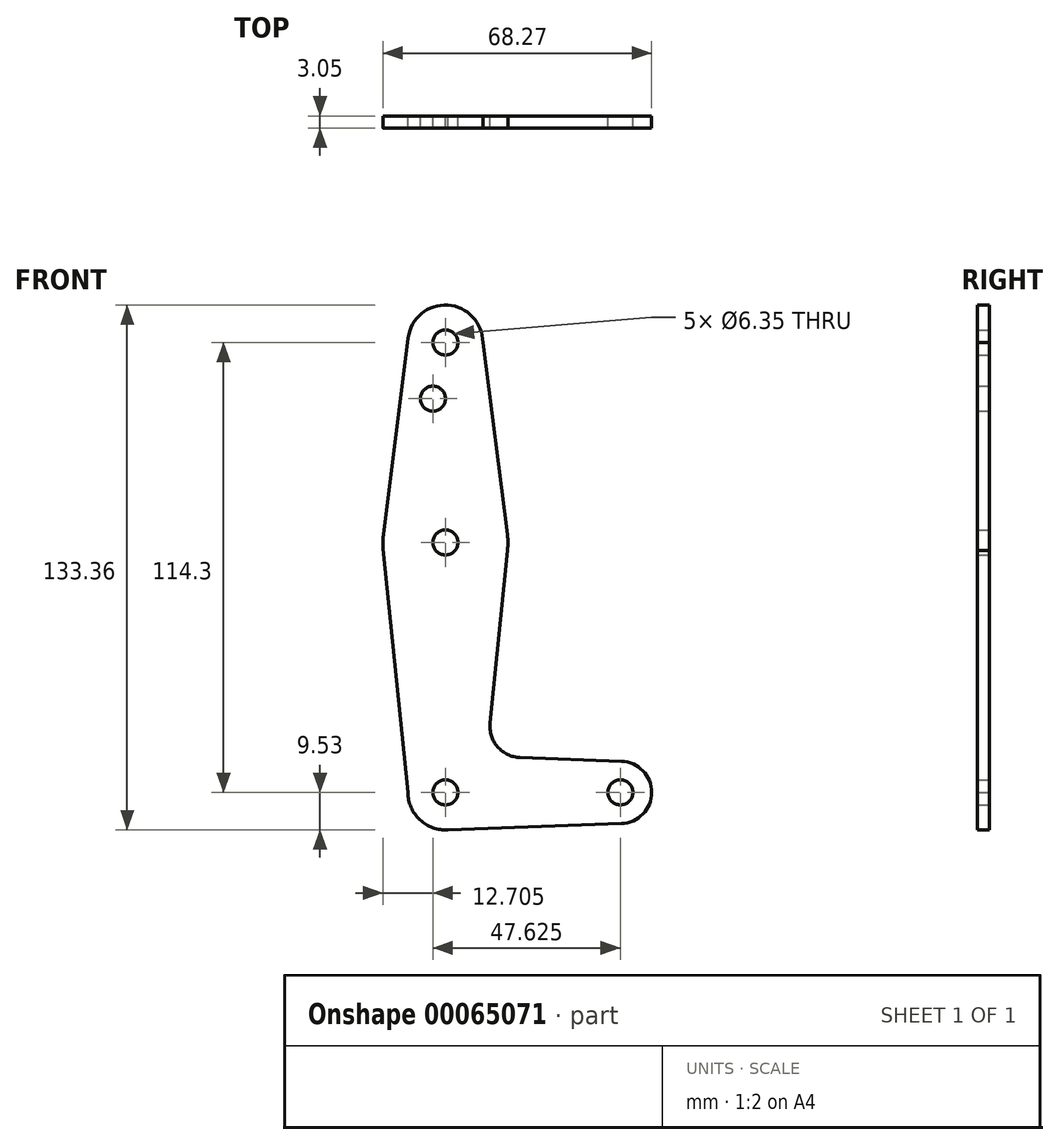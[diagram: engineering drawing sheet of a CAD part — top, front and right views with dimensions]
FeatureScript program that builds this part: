
annotation { "Feature Type Name" : "Feature", "Feature Type Description" : "" }
export const myFeature = defineFeature(function(context is Context, id is Id, definition is map)
    precondition{}
    {
        {
            var Q0;
            Q0=qCreatedBy(makeId("Front.planeOp"),FACE);
            var sketch = newSketch(context, id + "F0", { "sketchPlane" : qUnion([Q0])});
            skLineSegment(sketch, "E0", {"start": v(0, 114.3) * mm, "end": v(0, 0) * mm, "construction": true});
            skLineSegment(sketch, "E1", {"start": v(0, 0) * mm, "end": v(44.45, 0) * mm, "construction": true});
            skCircle(sketch, "E2", {"center": v(0, 114.3) * mm, "radius": 9.53 * mm});
            skCircle(sketch, "E3", {"center": v(0, 63.5) * mm, "radius": 15.88 * mm});
            skCircle(sketch, "E4", {"center": v(0, 0) * mm, "radius": 9.53 * mm});
            skCircle(sketch, "E5", {"center": v(44.45, 0) * mm, "radius": 7.94 * mm});
            skLineSegment(sketch, "E6", {"start": v(44.73, 7.93) * mm, "end": v(18.97, 8.85) * mm});
            skLineSegment(sketch, "E7", {"start": v(0, -9.52) * mm, "end": v(44.73, -7.93) * mm});
            skLineSegment(sketch, "E8", {"start": v(9.53, 114.3) * mm, "end": v(15.75, 65.5) * mm});
            skLineSegment(sketch, "E9", {"start": v(15.75, 61.5) * mm, "end": v(11.34, 17.6) * mm});
            skLineSegment(sketch, "E10", {"start": v(-9.53, 0) * mm, "end": v(-15.8, 61.9) * mm});
            skLineSegment(sketch, "E11", {"start": v(-9.45, 115.5) * mm, "end": v(-15.75, 65.48) * mm});
            skCircle(sketch, "E12", {"center": v(0, 114.3) * mm, "radius": 3.18 * mm});
            skCircle(sketch, "E13", {"center": v(0, 63.5) * mm, "radius": 3.18 * mm});
            skCircle(sketch, "E14", {"center": v(0, 0) * mm, "radius": 3.18 * mm});
            skCircle(sketch, "E15", {"center": v(44.45, 0) * mm, "radius": 3.18 * mm});
            skCircle(sketch, "E16", {"center": v(-3.17, 100.03) * mm, "radius": 3.18 * mm});
            skArc(sketch, "E17.filletArc", {"start": v(11.34, 17.6) * mm, "mid": v(13.26, 11.57) * mm, "end": v(18.97, 8.85) * mm});
            skSolve(sketch);
        }
        {
            var Q0;
            Q0 = qSketchRegion(id + "F0", true);
            extrude(context, id + "F1", {"entities" : qUnion([Q0]), "depth" : 3.05 * mm});
        }
    });
